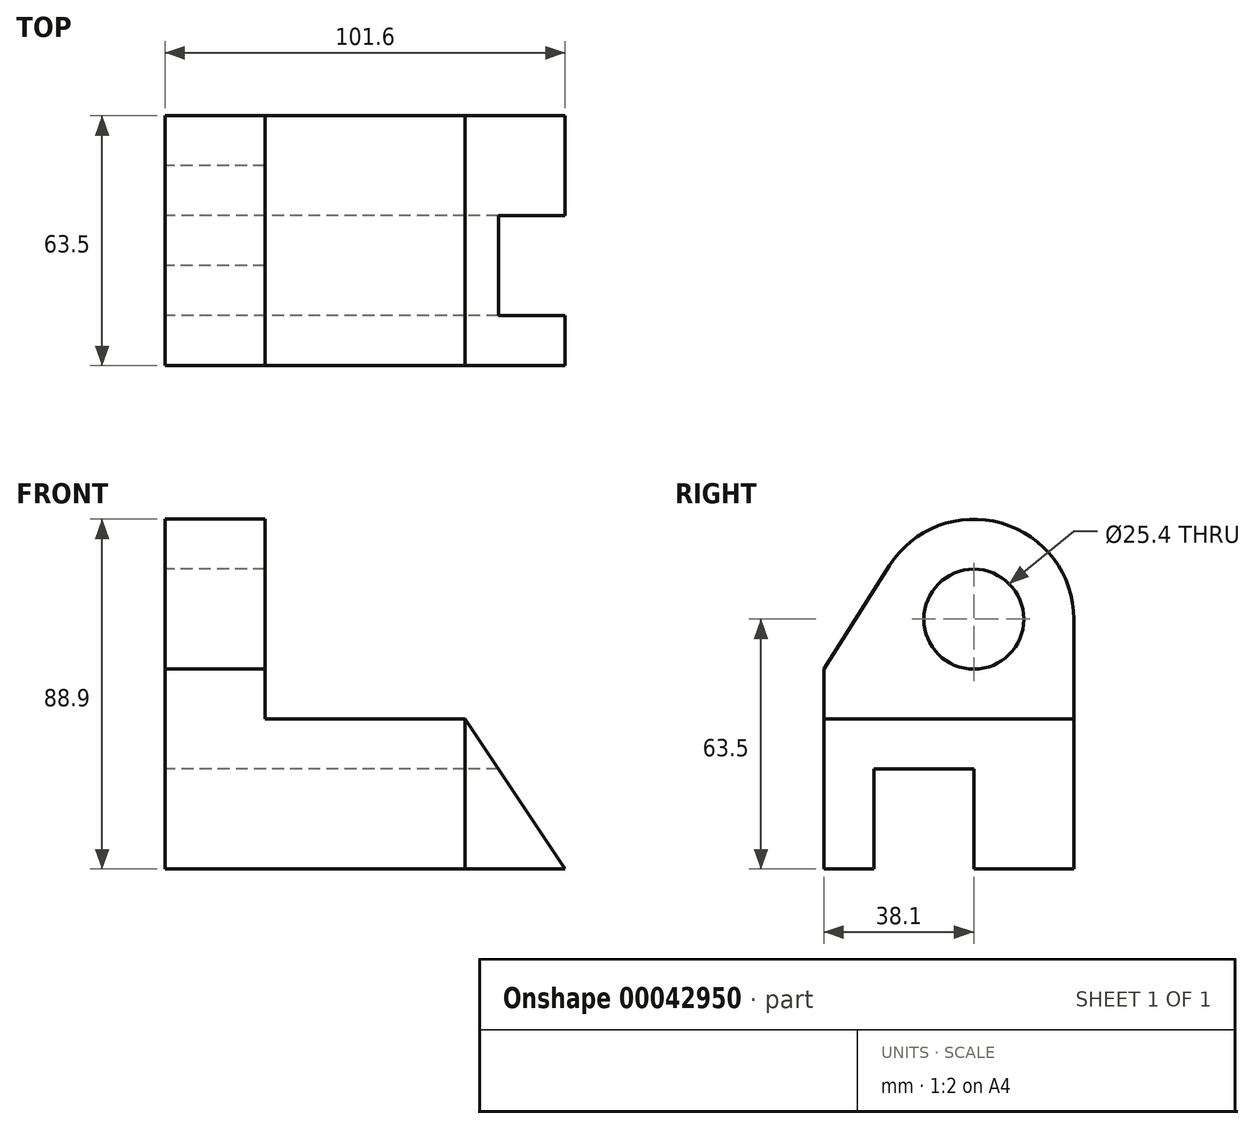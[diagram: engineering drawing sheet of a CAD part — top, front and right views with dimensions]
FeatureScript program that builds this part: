
annotation { "Feature Type Name" : "Feature", "Feature Type Description" : "" }
export const myFeature = defineFeature(function(context is Context, id is Id, definition is map)
    precondition{}
    {
        {
            var Q0;
            Q0=qCreatedBy(makeId("Top.planeOp"),FACE);
            var sketch = newSketch(context, id + "F0", { "sketchPlane" : qUnion([Q0])});
            skLineSegment(sketch, "E0.rect.bottom", {"start": v(50.8, 31.75) * mm, "end": v(-50.8, 31.75) * mm});
            skLineSegment(sketch, "E0.rect.top", {"start": v(50.8, -31.75) * mm, "end": v(-50.8, -31.75) * mm});
            skLineSegment(sketch, "E0.rect.left", {"start": v(50.8, 31.75) * mm, "end": v(50.8, -31.75) * mm});
            skLineSegment(sketch, "E0.rect.right", {"start": v(-50.8, 31.75) * mm, "end": v(-50.8, -31.75) * mm});
            skPoint(sketch, "E0.rect.middle", {"position": v(0, 0) * mm});
            skLineSegment(sketch, "E1", {"start": v(-50.8, 6.35) * mm, "end": v(50.8, 6.35) * mm});
            skLineSegment(sketch, "E2", {"start": v(-50.8, -19.05) * mm, "end": v(50.8, -19.05) * mm});
            skLineSegment(sketch, "E3", {"start": v(-25.4, 31.75) * mm, "end": v(-25.4, -31.75) * mm});
            skLineSegment(sketch, "E4", {"start": v(25.4, 31.75) * mm, "end": v(25.4, -31.75) * mm});
            skSolve(sketch);
        }
        {
            var Q0;
            {var subQ3=sQuery(id+"F0.wireOp",EDGE,"E0.rect.top");var subQ5=sQuery(id+"F0.wireOp",EDGE,"E3");var subQ7=makeQuery(id+"F0.imprint","INTERSECT",VERTEX,{"derivedFrom":[subQ3,subQ5]});Q0=makeQuery(id+"F0.imprint","IMPRINT",FACE,{"disambiguationData":[TD([[makeQuery(id+"F0.imprint","IMPRINT",EDGE,{"disambiguationData":[TD([[subQ7,1.0]])],"derivedFrom":subQ3}),-1.0]])]});}
            var Q1;
            {var subQ3=sQuery(id+"F0.wireOp",EDGE,"E1");var subQ5=sQuery(id+"F0.wireOp",EDGE,"E3");var subQ7=makeQuery(id+"F0.imprint","INTERSECT",VERTEX,{"derivedFrom":[subQ3,subQ5]});Q1=makeQuery(id+"F0.imprint","IMPRINT",FACE,{"disambiguationData":[TD([[makeQuery(id+"F0.imprint","IMPRINT",EDGE,{"disambiguationData":[TD([[subQ7,-1.0]])],"derivedFrom":subQ3}),-1.0]])]});}
            var Q2;
            {var subQ3=sQuery(id+"F0.wireOp",EDGE,"E0.rect.bottom");var subQ5=sQuery(id+"F0.wireOp",EDGE,"E3");var subQ7=makeQuery(id+"F0.imprint","INTERSECT",VERTEX,{"derivedFrom":[subQ3,subQ5]});Q2=makeQuery(id+"F0.imprint","IMPRINT",FACE,{"disambiguationData":[TD([[makeQuery(id+"F0.imprint","IMPRINT",EDGE,{"disambiguationData":[TD([[subQ7,1.0]])],"derivedFrom":subQ3}),1.0]])]});}
            extrude(context, id + "F1", {"entities" : qUnion([Q0, Q1, Q2]), "depth" : 38.1 * mm});
        }
        {
            var Q0;
            {var subQ3=sQuery(id+"F0.wireOp",EDGE,"E0.rect.right");var subQ5=sQuery(id+"F0.wireOp",EDGE,"E0.rect.bottom");var subQ6=makeQuery(id+"F0.imprint","INTERSECT",VERTEX,{"derivedFrom":[subQ5,subQ3]});Q0=makeQuery(id+"F0.imprint","IMPRINT",FACE,{"disambiguationData":[TD([[makeQuery(id+"F0.imprint","IMPRINT",EDGE,{"disambiguationData":[TD([[subQ6,1.0]])],"derivedFrom":subQ5}),1.0]])]});}
            var Q1;
            {var subQ3=sQuery(id+"F0.wireOp",EDGE,"E1");var subQ5=sQuery(id+"F0.wireOp",EDGE,"E0.rect.right");var subQ7=makeQuery(id+"F0.imprint","INTERSECT",VERTEX,{"derivedFrom":[subQ5,subQ3]});Q1=makeQuery(id+"F0.imprint","IMPRINT",FACE,{"disambiguationData":[TD([[makeQuery(id+"F0.imprint","IMPRINT",EDGE,{"disambiguationData":[TD([[subQ7,-1.0]])],"derivedFrom":subQ5}),1.0]])]});}
            var Q2;
            {var subQ3=sQuery(id+"F0.wireOp",EDGE,"E0.rect.right");var subQ5=sQuery(id+"F0.wireOp",EDGE,"E0.rect.top");var subQ6=makeQuery(id+"F0.imprint","INTERSECT",VERTEX,{"derivedFrom":[subQ5,subQ3]});Q2=makeQuery(id+"F0.imprint","IMPRINT",FACE,{"disambiguationData":[TD([[makeQuery(id+"F0.imprint","IMPRINT",EDGE,{"disambiguationData":[TD([[subQ6,1.0]])],"derivedFrom":subQ5}),-1.0]])]});}
            extrude(context, id + "F2", {"entities" : qUnion([Q0, Q1, Q2]), "operationType" : NewBodyOperationType.ADD, "depth" : 50.8 * mm});
        }
        {
            var Q0;
            {var subQ0=sQuery(id+"F0.wireOp",EDGE,"E0.rect.top");Q0=makeQuery(id+"F2.boolean.opBoolean","MERGE",FACE,{"derivedFrom":[makeQuery(id+"F1.opExtrude","SWEPT_FACE",FACE,{"disambiguationData":[OSD([subQ0])]}),makeQuery(id+"F2.opExtrude","SWEPT_FACE",FACE,{"disambiguationData":[OSD([subQ0])]})]});}
            var sketch = newSketch(context, id + "F3", { "sketchPlane" : qUnion([Q0])});
            skLineSegment(sketch, "E5", {"start": v(25.4, 38.1) * mm, "end": v(25.4, 0) * mm});
            skLineSegment(sketch, "E6", {"start": v(25.4, 0) * mm, "end": v(50.8, 0) * mm});
            skLineSegment(sketch, "E7", {"start": v(50.8, 0) * mm, "end": v(25.4, 38.1) * mm});
            skSolve(sketch);
        }
        {
            var Q0;
            Q0=makeQuery(id+"F1.opExtrude","SWEPT_FACE",FACE,{"disambiguationData":[OSD([sQuery(id+"F0.wireOp",EDGE,"E4")])]});
            var sketch = newSketch(context, id + "F4", { "sketchPlane" : qUnion([Q0])});
            skLineSegment(sketch, "E8", {"start": v(6.35, 0) * mm, "end": v(6.35, 25.4) * mm});
            skLineSegment(sketch, "E9", {"start": v(6.35, 25.4) * mm, "end": v(-19.05, 25.4) * mm});
            skLineSegment(sketch, "E10", {"start": v(-19.05, 25.4) * mm, "end": v(-19.05, 0) * mm});
            skLineSegment(sketch, "E11", {"start": v(-19.05, 0) * mm, "end": v(6.35, 0) * mm});
            skSolve(sketch);
        }
        {
            var Q0;
            Q0=makeQuery(id+"F3.imprint","IMPRINT",FACE,{"disambiguationData":[TD([[makeQuery(id+"F3.imprint","IMPRINT",EDGE,{"derivedFrom":sQuery(id+"F3.wireOp",EDGE,"E5")}),1.0]])]});
            extrude(context, id + "F5", {"entities" : qUnion([Q0]), "oppositeDirection" : true, "depth" : 63.5 * mm});
        }
        {
            var Q0;
            Q0 = qSketchRegion(id + "F4", true);
            extrude(context, id + "F6", {"entities" : qUnion([Q0]), "operationType" : NewBodyOperationType.REMOVE, "endBound" : BoundingType.SYMMETRIC, "depth" : 177.8 * mm});
        }
        {
            var Q0;
            Q0=makeQuery(id+"F2.opExtrude","SWEPT_FACE",FACE,{"disambiguationData":[OSD([sQuery(id+"F0.wireOp",EDGE,"E0.rect.right")])]});
            var sketch = newSketch(context, id + "F7", { "sketchPlane" : qUnion([Q0])});
            skLineSegment(sketch, "E12", {"start": v(19.05, 50.8) * mm, "end": v(31.75, 50.8) * mm});
            skCircle(sketch, "E13", {"center": v(-6.35, 63.5) * mm, "radius": 12.7 * mm});
            skCircle(sketch, "E14", {"center": v(-6.35, 63.5) * mm, "radius": 25.4 * mm});
            skLineSegment(sketch, "E15", {"start": v(-31.75, 50.8) * mm, "end": v(-31.75, 63.5) * mm});
            skLineSegment(sketch, "E16", {"start": v(-31.75, 50.8) * mm, "end": v(19.05, 50.8) * mm});
            skLineSegment(sketch, "E17", {"start": v(31.75, 50.8) * mm, "end": v(15.11, 77.09) * mm});
            skSolve(sketch);
        }
        {
            var Q0;
            Q0 = qSketchRegion(id + "F7", true);
            extrude(context, id + "F8", {"entities" : qUnion([Q0]), "operationType" : NewBodyOperationType.ADD, "oppositeDirection" : true, "depth" : 25.4 * mm});
        }
    });
